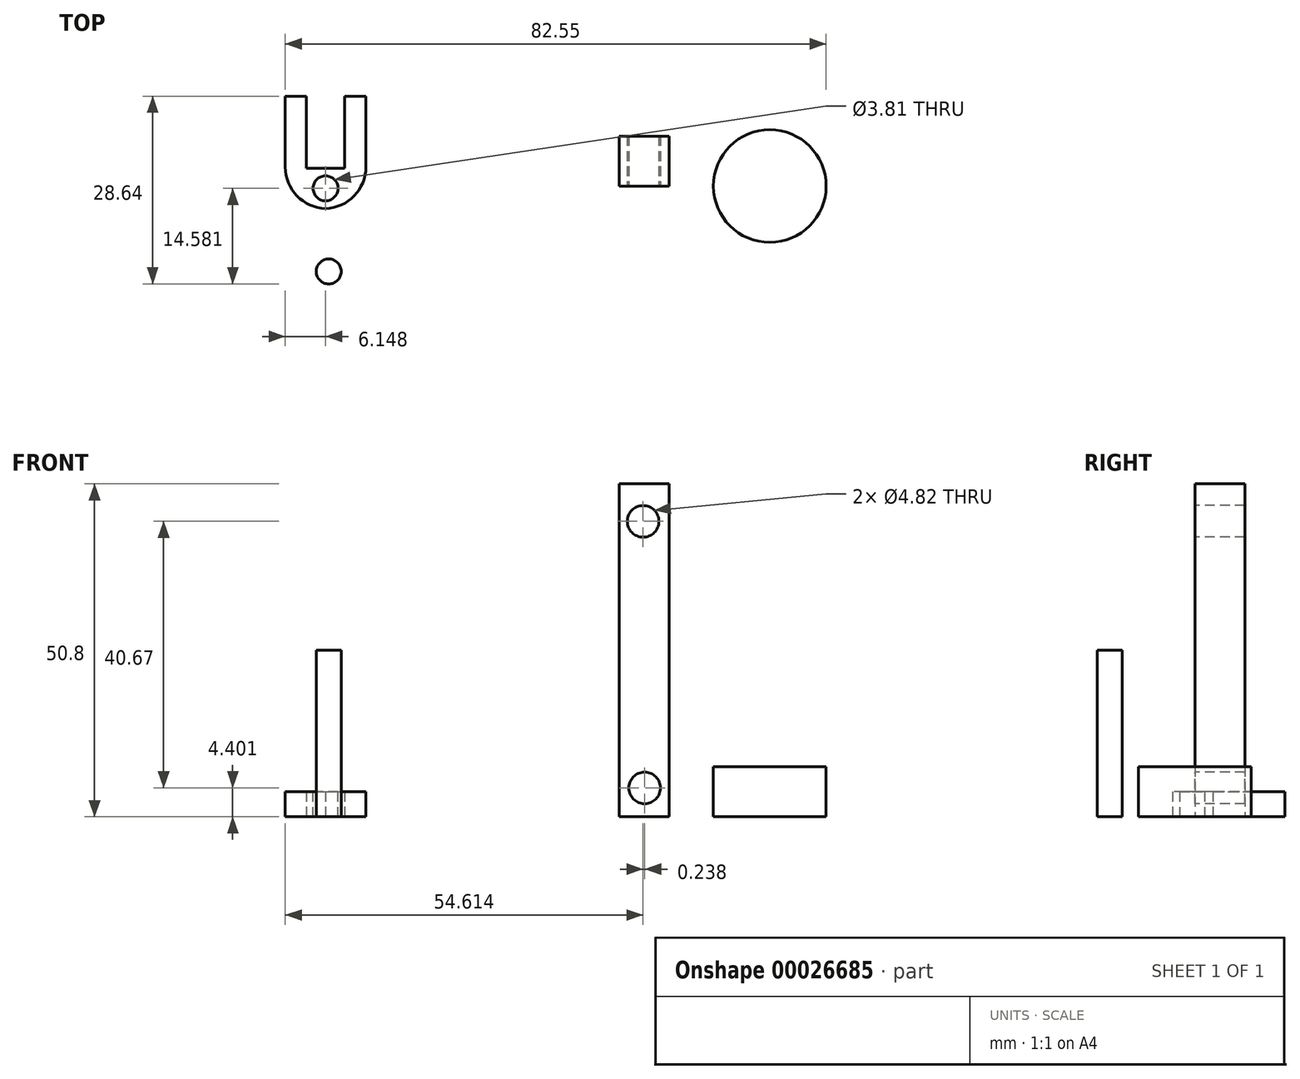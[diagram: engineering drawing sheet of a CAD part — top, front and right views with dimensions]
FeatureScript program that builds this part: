
annotation { "Feature Type Name" : "Feature", "Feature Type Description" : "" }
export const myFeature = defineFeature(function(context is Context, id is Id, definition is map)
    precondition{}
    {
        {
            var Q0;
            Q0=qCreatedBy(makeId("Top.planeOp"),FACE);
            var sketch = newSketch(context, id + "F0", { "sketchPlane" : qUnion([Q0])});
            skLineSegment(sketch, "E0.bottom", {"start": v(0, 0) * mm, "end": v(-7.62, 0) * mm});
            skLineSegment(sketch, "E0.top", {"start": v(0, 7.62) * mm, "end": v(-7.62, 7.62) * mm});
            skLineSegment(sketch, "E0.left", {"start": v(0, 0) * mm, "end": v(0, 7.62) * mm});
            skLineSegment(sketch, "E0.right", {"start": v(-7.62, 0) * mm, "end": v(-7.62, 7.62) * mm});
            skSolve(sketch);
        }
        {
            var Q0;
            Q0=makeQuery(id+"F0.imprint","IMPRINT",FACE,{"disambiguationData":[TD([[makeQuery(id+"F0.imprint","IMPRINT",EDGE,{"derivedFrom":sQuery(id+"F0.wireOp",EDGE,"376d1727-07ca-4b6f-8c5d-407781719f30")}),1.0]])]});
            var Q1;
            Q1=makeQuery(id+"F0.imprint","IMPRINT",FACE,{"disambiguationData":[TD([[makeQuery(id+"F0.imprint","IMPRINT",EDGE,{"derivedFrom":sQuery(id+"F0.wireOp",EDGE,"E0.bottom")}),-1.0]])]});
            extrude(context, id + "F1", {"entities" : qUnion([Q0, Q1]), "depth" : 50.8 * mm});
        }
        {
            var Q0;
            Q0=qCreatedBy(makeId("Top.planeOp"),FACE);
            var sketch = newSketch(context, id + "F2", { "sketchPlane" : qUnion([Q0])});
            skCircle(sketch, "E1", {"center": v(15.37, 0) * mm, "radius": 8.6 * mm});
            skSolve(sketch);
        }
        {
            var Q0;
            Q0=makeQuery(id+"F2.imprint","IMPRINT",FACE,{"disambiguationData":[TD([[makeQuery(id+"F2.imprint","IMPRINT",EDGE,{"derivedFrom":sQuery(id+"F2.wireOp",EDGE,"E1")}),1.0]])]});
            extrude(context, id + "F3", {"entities" : qUnion([Q0]), "depth" : 7.62 * mm});
        }
        {
            var Q0;
            Q0=qCreatedBy(makeId("Top.planeOp"),FACE);
            var sketch = newSketch(context, id + "F4", { "sketchPlane" : qUnion([Q0])});
            skCircle(sketch, "E2", {"center": v(-51.95, -13.03) * mm, "radius": 1.9 * mm});
            skSolve(sketch);
        }
        {
            var Q0;
            Q0 = qSketchRegion(id + "F4", true);
            extrude(context, id + "F5", {"entities" : qUnion([Q0]), "depth" : 25.4 * mm});
        }
        {
            var Q0;
            Q0=makeQuery(id+"F1.opExtrude","SWEPT_FACE",FACE,{"disambiguationData":[OSD([sQuery(id+"F0.wireOp",EDGE,"E0.bottom")])]});
            var sketch = newSketch(context, id + "F6", { "sketchPlane" : qUnion([Q0])});
            skCircle(sketch, "E3", {"center": v(-3.97, 45.07) * mm, "radius": 2.41 * mm});
            skCircle(sketch, "E4", {"center": v(-3.73, 4.4) * mm, "radius": 2.41 * mm});
            skSolve(sketch);
        }
        {
            var Q0;
            Q0=makeQuery(id+"F6.imprint","IMPRINT",FACE,{"disambiguationData":[TD([[makeQuery(id+"F6.imprint","IMPRINT",EDGE,{"derivedFrom":sQuery(id+"F6.wireOp",EDGE,"E3")}),1.0]])]});
            var Q1;
            Q1=makeQuery(id+"F6.imprint","IMPRINT",FACE,{"disambiguationData":[TD([[makeQuery(id+"F6.imprint","IMPRINT",EDGE,{"derivedFrom":sQuery(id+"F6.wireOp",EDGE,"E4")}),1.0]])]});
            extrude(context, id + "F7", {"entities" : qUnion([Q0, Q1]), "operationType" : NewBodyOperationType.REMOVE, "oppositeDirection" : true, "depth" : 25.4 * mm});
        }
        {
            var Q0;
            Q0=qCreatedBy(makeId("Top.planeOp"),FACE);
            var sketch = newSketch(context, id + "F8", { "sketchPlane" : qUnion([Q0])});
            skLineSegment(sketch, "E5", {"start": v(-58.58, 13.7) * mm, "end": v(-58.58, 2.92) * mm});
            skLineSegment(sketch, "E6", {"start": v(-52.63, -3.43) * mm, "end": v(-52.23, -3.43) * mm});
            skLineSegment(sketch, "E7", {"start": v(-46.28, 2.92) * mm, "end": v(-46.28, 13.7) * mm});
            skLineSegment(sketch, "E8", {"start": v(-46.28, 13.7) * mm, "end": v(-49.5, 13.7) * mm});
            skLineSegment(sketch, "E9", {"start": v(-58.58, 13.7) * mm, "end": v(-55.37, 13.7) * mm});
            skPoint(sketch, "E10.visualSharp", {"position": v(-58.58, -3.43) * mm});
            skArc(sketch, "E10.filletArc", {"start": v(-58.58, 2.92) * mm, "mid": v(-56.73, -1.57) * mm, "end": v(-52.23, -3.43) * mm});
            skPoint(sketch, "E11.visualSharp", {"position": v(-46.28, -3.43) * mm});
            skArc(sketch, "E11.filletArc", {"start": v(-52.63, -3.43) * mm, "mid": v(-48.14, -1.57) * mm, "end": v(-46.28, 2.92) * mm});
            skLineSegment(sketch, "E12", {"start": v(-55.37, 13.7) * mm, "end": v(-55.37, 2.72) * mm});
            skLineSegment(sketch, "E13", {"start": v(-55.37, 2.72) * mm, "end": v(-49.5, 2.72) * mm});
            skLineSegment(sketch, "E14", {"start": v(-49.5, 2.72) * mm, "end": v(-49.5, 13.7) * mm});
            skSolve(sketch);
        }
        {
            var Q0;
            {var subQ4=sQuery(id+"F8.wireOp",EDGE,"E5");Q0=makeQuery(id+"F8.imprint","IMPRINT",FACE,{"disambiguationData":[TD([[makeQuery(id+"F8.imprint","IMPRINT",EDGE,{"derivedFrom":subQ4}),1.0]])]});}
            extrude(context, id + "F9", {"entities" : qUnion([Q0]), "depth" : 3.8 * mm});
        }
        {
            var Q0;
            Q0=makeQuery(id+"F9.opExtrude","CAP_FACE",FACE,{"disambiguationData":[OSD([sQuery(id+"F8.wireOp",EDGE,"E5"),sQuery(id+"F8.wireOp",EDGE,"E7"),sQuery(id+"F8.wireOp",EDGE,"E8"),sQuery(id+"F8.wireOp",EDGE,"E9"),sQuery(id+"F8.wireOp",EDGE,"E10.filletArc"),sQuery(id+"F8.wireOp",EDGE,"E11.filletArc"),sQuery(id+"F8.wireOp",EDGE,"E12"),sQuery(id+"F8.wireOp",EDGE,"E13"),sQuery(id+"F8.wireOp",EDGE,"E14")])],"isStart":false});
            var sketch = newSketch(context, id + "F10", { "sketchPlane" : qUnion([Q0])});
            skLineSegment(sketch, "E15", {"start": v(-52.43, 2.72) * mm, "end": v(-52.43, -3.42) * mm});
            skCircle(sketch, "E16", {"center": v(-52.43, -0.35) * mm, "radius": 1.9 * mm});
            skSolve(sketch);
        }
        {
            var Q0;
            {var subQ0=sQuery(id+"F10.wireOp",EDGE,"E16");var subQ1=sQuery(id+"F10.wireOp",EDGE,"E15");var subQ3=makeQuery(id+"F10.imprint","INTERSECT",VERTEX,{"disambiguationData":[OD(0.0)],"derivedFrom":[subQ1,subQ0]});Q0=makeQuery(id+"F10.imprint","IMPRINT",FACE,{"disambiguationData":[TD([[makeQuery(id+"F10.imprint","IMPRINT",EDGE,{"disambiguationData":[TD([[subQ3,-1.0]])],"derivedFrom":subQ1}),1.0]])]});}
            var Q1;
            {var subQ0=sQuery(id+"F10.wireOp",EDGE,"E16");var subQ1=sQuery(id+"F10.wireOp",EDGE,"E15");var subQ3=makeQuery(id+"F10.imprint","INTERSECT",VERTEX,{"disambiguationData":[OD(0.0)],"derivedFrom":[subQ1,subQ0]});Q1=makeQuery(id+"F10.imprint","IMPRINT",FACE,{"disambiguationData":[TD([[makeQuery(id+"F10.imprint","IMPRINT",EDGE,{"disambiguationData":[TD([[subQ3,-1.0]])],"derivedFrom":subQ1}),-1.0]])]});}
            extrude(context, id + "F11", {"entities" : qUnion([Q0, Q1]), "operationType" : NewBodyOperationType.REMOVE, "oppositeDirection" : true, "depth" : 25.4 * mm});
        }
    });
